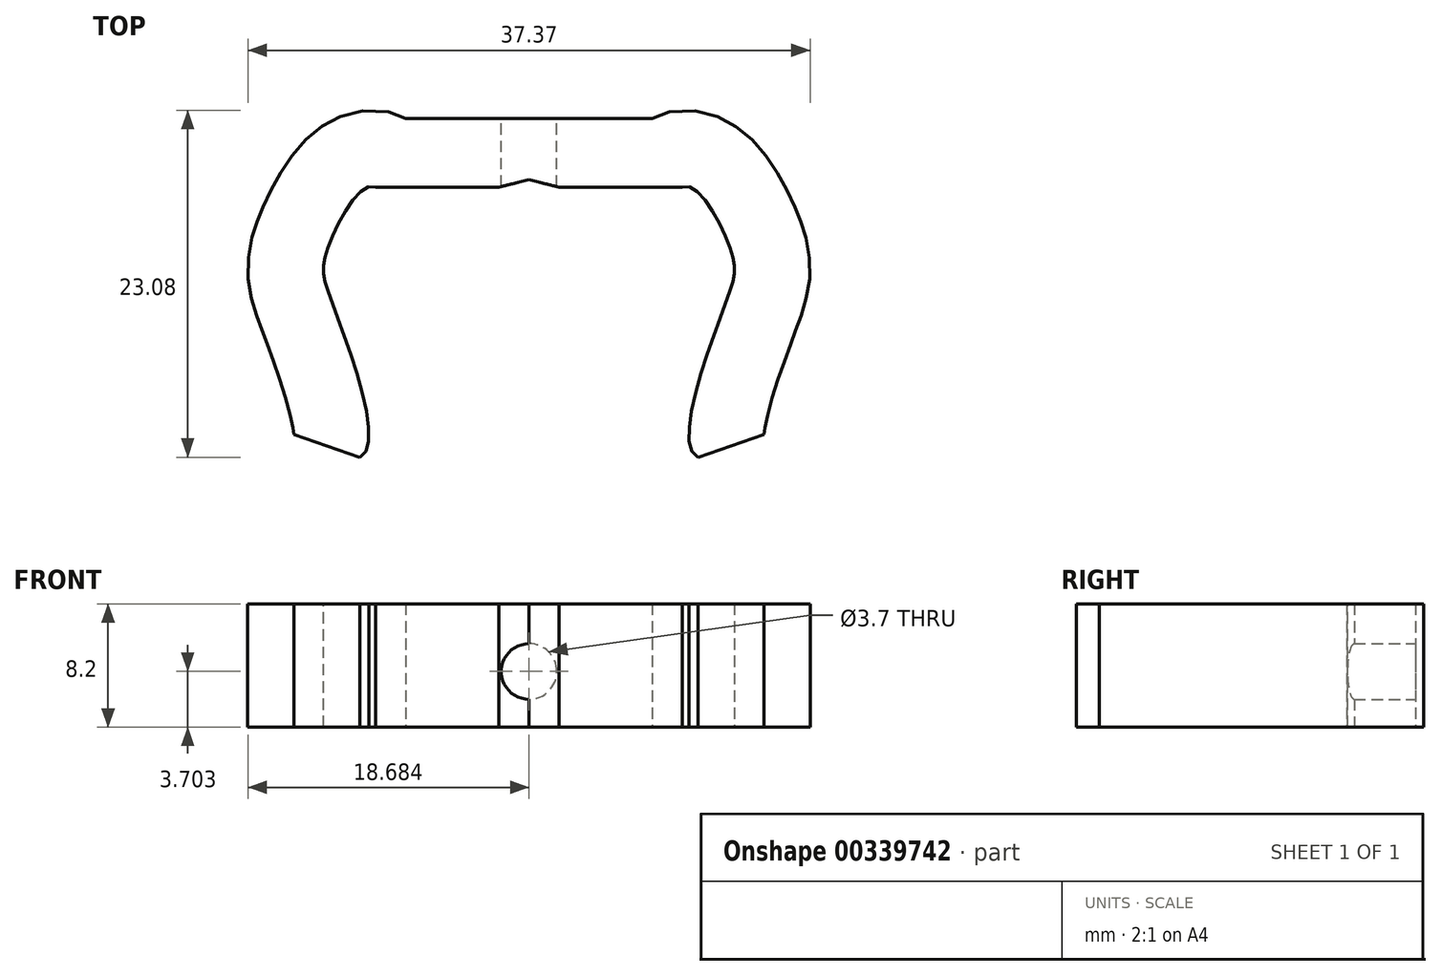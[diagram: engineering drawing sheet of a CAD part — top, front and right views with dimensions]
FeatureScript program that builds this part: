
annotation { "Feature Type Name" : "Feature", "Feature Type Description" : "" }
export const myFeature = defineFeature(function(context is Context, id is Id, definition is map)
    precondition{}
    {
        {
            var Q0;
            Q0=qCreatedBy(makeId("Top.planeOp"),FACE);
            var sketch = newSketch(context, id + "F0", { "sketchPlane" : qUnion([Q0])});
            skLineSegment(sketch, "E0", {"start": v(-35.03, 22.65) * mm, "end": v(-26.83, 22.65) * mm});
            skLineSegment(sketch, "E1", {"start": v(-37.04, 23.14) * mm, "end": v(-35.03, 22.65) * mm});
            skFitSpline(sketch, "E2.MirrorCS", {"points": [v(-26.83, 22.65) * mm, v(-23.66, 18.6) * mm, v(-23.98, 14.9) * mm, v(-25.8, 4.68) * mm, v(-24.5, 6.78) * mm], "startDerivative": vector(12.57, 5.66) * mm, "endDerivative": vector(-24.51, 25.72) * mm});
            skLineSegment(sketch, "E3", {"start": v(-26.83, 22.65) * mm, "end": v(-26.83, 22.65) * mm});
            skFitSpline(sketch, "E4.0", {"points": [v(-28.88, 27.2) * mm, v(-28.44, 27.4) * mm, v(-27.48, 27.7) * mm, v(-26.04, 27.73) * mm, v(-24.84, 27.46) * mm, v(-23.9, 27.06) * mm, v(-23.18, 26.62) * mm, v(-22.44, 26.03) * mm, v(-21.76, 25.34) * mm, v(-21.15, 24.55) * mm, v(-20.64, 23.8) * mm, v(-20.2, 23.04) * mm, v(-19.82, 22.3) * mm, v(-19.48, 21.58) * mm, v(-19.23, 21) * mm, v(-19.05, 20.54) * mm, v(-18.88, 20.1) * mm, v(-18.69, 19.5) * mm, v(-18.5, 18.67) * mm, v(-18.37, 17.74) * mm, v(-18.36, 16.77) * mm, v(-18.47, 15.86) * mm, v(-18.65, 15.07) * mm, v(-18.85, 14.4) * mm, v(-19.05, 13.81) * mm, v(-19.23, 13.33) * mm, v(-19.38, 12.94) * mm, v(-19.53, 12.52) * mm, v(-19.74, 11.96) * mm, v(-20, 11.25) * mm, v(-20.26, 10.5) * mm, v(-20.51, 9.75) * mm, v(-20.75, 9) * mm, v(-20.97, 8.28) * mm, v(-21.15, 7.6) * mm, v(-21.26, 7.1) * mm, v(-21.33, 6.77) * mm, v(-21.37, 6.54) * mm, v(-21.39, 6.4) * mm, v(-21.4, 6.3) * mm, v(-21.4, 6.24) * mm, v(-21.4, 6.2) * mm, v(-21.4, 6.19) * mm, v(-21.4, 6.18) * mm, v(-21.4, 6.17) * mm, v(-21.4, 6.17) * mm, v(-21.4, 6.17) * mm, v(-21.4, 6.17) * mm, v(-21.4, 6.17) * mm, v(-21.4, 6.17) * mm, v(-21.4, 6.16) * mm, v(-21.4, 6.15) * mm, v(-21.4, 6.13) * mm, v(-21.4, 6.1) * mm, v(-21.4, 6.05) * mm, v(-21.4, 6) * mm, v(-21.4, 5.98) * mm]});
            skLineSegment(sketch, "E5", {"start": v(-28.84, 27.23) * mm, "end": v(-37.04, 27.23) * mm});
            skLineSegment(sketch, "E6", {"start": v(-37.04, 27.23) * mm, "end": v(-37.04, 23.14) * mm});
            skLineSegment(sketch, "E7.MirrorCS", {"start": v(-37.04, 23.14) * mm, "end": v(-39.04, 22.65) * mm});
            skLineSegment(sketch, "E8.MirrorCS", {"start": v(-47.24, 22.65) * mm, "end": v(-47.24, 22.65) * mm});
            skLineSegment(sketch, "E9.MirrorCS", {"start": v(-45.24, 27.23) * mm, "end": v(-37.04, 27.23) * mm});
            skLineSegment(sketch, "E10.MirrorCS", {"start": v(-39.04, 22.65) * mm, "end": v(-47.24, 22.65) * mm});
            skFitSpline(sketch, "E11.MirrorCS", {"points": [v(-47.24, 22.65) * mm, v(-50.4, 18.6) * mm, v(-50.1, 14.9) * mm, v(-48.28, 4.68) * mm, v(-49.58, 6.78) * mm], "startDerivative": vector(-12.57, 5.66) * mm, "endDerivative": vector(24.51, 25.72) * mm});
            skFitSpline(sketch, "E12.0", {"points": [v(-45.2, 27.2) * mm, v(-45.63, 27.4) * mm, v(-46.6, 27.7) * mm, v(-48.03, 27.73) * mm, v(-49.24, 27.46) * mm, v(-50.17, 27.06) * mm, v(-50.89, 26.62) * mm, v(-51.63, 26.03) * mm, v(-52.3, 25.34) * mm, v(-52.92, 24.55) * mm, v(-53.43, 23.8) * mm, v(-53.87, 23.04) * mm, v(-54.25, 22.3) * mm, v(-54.6, 21.58) * mm, v(-54.84, 21) * mm, v(-55.02, 20.54) * mm, v(-55.19, 20.1) * mm, v(-55.38, 19.5) * mm, v(-55.58, 18.67) * mm, v(-55.7, 17.74) * mm, v(-55.71, 16.77) * mm, v(-55.6, 15.86) * mm, v(-55.42, 15.07) * mm, v(-55.22, 14.4) * mm, v(-55.02, 13.81) * mm, v(-54.84, 13.33) * mm, v(-54.7, 12.94) * mm, v(-54.54, 12.52) * mm, v(-54.34, 11.96) * mm, v(-54.08, 11.25) * mm, v(-53.82, 10.5) * mm, v(-53.56, 9.75) * mm, v(-53.32, 9) * mm, v(-53.1, 8.28) * mm, v(-52.92, 7.6) * mm, v(-52.8, 7.1) * mm, v(-52.74, 6.77) * mm, v(-52.7, 6.54) * mm, v(-52.68, 6.4) * mm, v(-52.67, 6.3) * mm, v(-52.67, 6.24) * mm, v(-52.67, 6.2) * mm, v(-52.67, 6.19) * mm, v(-52.67, 6.18) * mm, v(-52.67, 6.17) * mm, v(-52.67, 6.17) * mm, v(-52.67, 6.17) * mm, v(-52.67, 6.17) * mm, v(-52.67, 6.17) * mm, v(-52.67, 6.17) * mm, v(-52.67, 6.16) * mm, v(-52.67, 6.15) * mm, v(-52.67, 6.13) * mm, v(-52.67, 6.1) * mm, v(-52.67, 6.05) * mm, v(-52.67, 6) * mm, v(-52.67, 5.98) * mm]});
            skLineSegment(sketch, "E13", {"start": v(-45.24, 27.23) * mm, "end": v(-45.24, 29.23) * mm});
            skLineSegment(sketch, "E14", {"start": v(-28.84, 27.23) * mm, "end": v(-28.84, 29.23) * mm});
            skLineSegment(sketch, "E15", {"start": v(-25.8, 4.68) * mm, "end": v(-21.4, 6.19) * mm});
            skLineSegment(sketch, "E16", {"start": v(-48.28, 4.68) * mm, "end": v(-52.67, 6.19) * mm});
            skLineSegment(sketch, "E17", {"start": v(-45.24, 27.23) * mm, "end": v(-45.38, 27.29) * mm});
            skLineSegment(sketch, "E18", {"start": v(-49.88, 5.12) * mm, "end": v(-52.67, 6.19) * mm});
            skLineSegment(sketch, "E19", {"start": v(-21.4, 6.19) * mm, "end": v(-21.4, 6.19) * mm});
            skLineSegment(sketch, "E20", {"start": v(-52.67, 6.19) * mm, "end": v(-52.67, 6.2) * mm});
            skSolve(sketch);
        }
        {
            var Q0;
            Q0=makeQuery(id+"F0.imprint","IMPRINT",FACE,{"disambiguationData":[TD([[makeQuery(id+"F0.imprint","IMPRINT",EDGE,{"derivedFrom":sQuery(id+"F0.wireOp",EDGE,"E6")}),-1.0]])]});
            var Q1;
            Q1=makeQuery(id+"F0.imprint","IMPRINT",FACE,{"disambiguationData":[TD([[makeQuery(id+"F0.imprint","IMPRINT",EDGE,{"derivedFrom":sQuery(id+"F0.wireOp",EDGE,"E0")}),1.0]])]});
            var Q2;
            Q2=makeQuery(id+"F0.imprint","IMPRINT",FACE,{"disambiguationData":[TD([[makeQuery(id+"F0.imprint","IMPRINT",EDGE,{"derivedFrom":sQuery(id+"F0.wireOp",EDGE,"E5")}),-1.0]])]});
            extrude(context, id + "F1", {"entities" : qUnion([Q0, Q1, Q2]), "depth" : 8.2 * mm});
        }
        {
            var Q0;
            Q0=makeQuery(id+"F1.opExtrude","SWEPT_FACE",FACE,{"disambiguationData":[OSD([sQuery(id+"F0.wireOp",EDGE,"E5"),sQuery(id+"F0.wireOp",EDGE,"E9.MirrorCS")])]});
            var sketch = newSketch(context, id + "F2", { "sketchPlane" : qUnion([Q0])});
            skCircle(sketch, "E21", {"center": v(37.04, 3.7) * mm, "radius": 1.85 * mm});
            skPoint(sketch, "E21.centerSnap0", {"position": v(37.04, 0) * mm});
            skSolve(sketch);
        }
        {
            var Q0;
            Q0=makeQuery(id+"F2.imprint","IMPRINT",FACE,{"disambiguationData":[TD([[makeQuery(id+"F2.imprint","IMPRINT",EDGE,{"derivedFrom":sQuery(id+"F2.wireOp",EDGE,"E21")}),1.0]])]});
            extrude(context, id + "F3", {"entities" : qUnion([Q0]), "operationType" : NewBodyOperationType.REMOVE, "oppositeDirection" : true, "depth" : 25 * mm});
        }
    });
